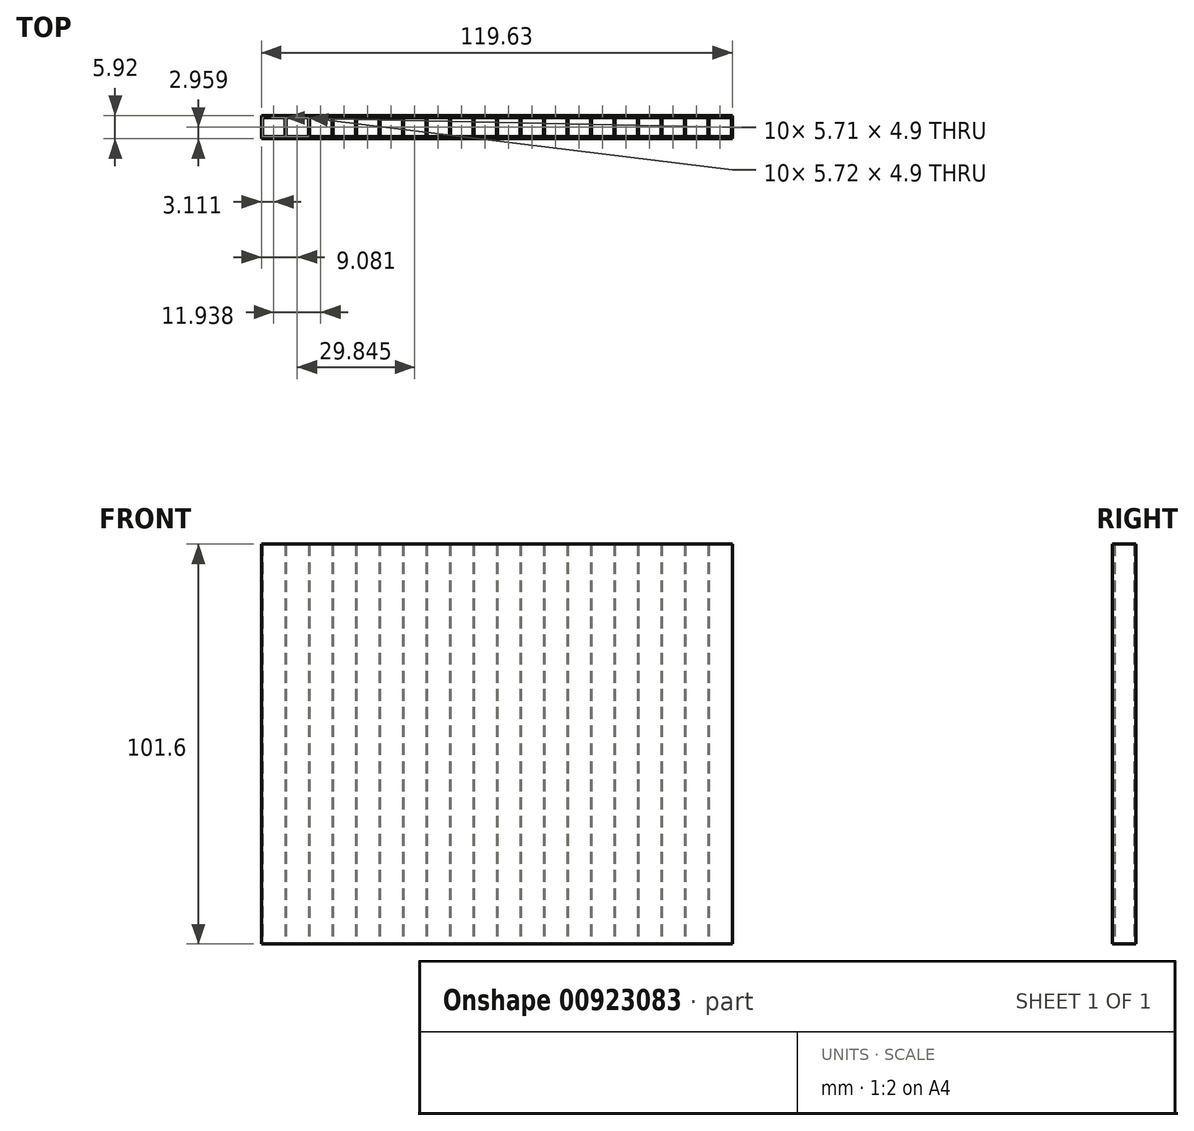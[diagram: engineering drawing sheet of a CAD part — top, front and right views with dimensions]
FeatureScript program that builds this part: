
annotation { "Feature Type Name" : "Feature", "Feature Type Description" : "" }
export const myFeature = defineFeature(function(context is Context, id is Id, definition is map)
    precondition{}
    {
        {
            var Q0;
            Q0=qCreatedBy(makeId("Top.planeOp"),FACE);
            var sketch = newSketch(context, id + "F0", { "sketchPlane" : qUnion([Q0])});
            skLineSegment(sketch, "E0", {"start": v(0, 0) * mm, "end": v(119.63, 0) * mm});
            skLineSegment(sketch, "E1", {"start": v(119.63, 0) * mm, "end": v(119.63, 5.92) * mm});
            skLineSegment(sketch, "E2", {"start": v(119.63, 5.92) * mm, "end": v(0, 5.92) * mm});
            skLineSegment(sketch, "E3", {"start": v(0, 5.92) * mm, "end": v(0, 0) * mm});
            skLineSegment(sketch, "E4.bottom", {"start": v(0.25, 5.41) * mm, "end": v(5.97, 5.41) * mm});
            skLineSegment(sketch, "E4.top", {"start": v(0.25, 0.5) * mm, "end": v(5.97, 0.5) * mm});
            skLineSegment(sketch, "E4.left", {"start": v(0.25, 5.41) * mm, "end": v(0.25, 0.5) * mm});
            skLineSegment(sketch, "E4.right", {"start": v(5.97, 5.41) * mm, "end": v(5.97, 0.5) * mm});
            skLineSegment(sketch, "E5.1.0.0", {"start": v(6.22, 5.41) * mm, "end": v(6.22, 0.5) * mm});
            skLineSegment(sketch, "E5.1.0.1", {"start": v(6.22, 5.41) * mm, "end": v(11.94, 5.41) * mm});
            skLineSegment(sketch, "E5.1.0.2", {"start": v(11.94, 5.41) * mm, "end": v(11.94, 0.5) * mm});
            skLineSegment(sketch, "E5.1.0.3", {"start": v(6.22, 0.5) * mm, "end": v(11.94, 0.5) * mm});
            skLineSegment(sketch, "E5.2.0.0", {"start": v(12.2, 5.41) * mm, "end": v(12.2, 0.5) * mm});
            skLineSegment(sketch, "E5.2.0.1", {"start": v(12.2, 5.41) * mm, "end": v(17.9, 5.41) * mm});
            skLineSegment(sketch, "E5.2.0.2", {"start": v(17.9, 5.41) * mm, "end": v(17.9, 0.5) * mm});
            skLineSegment(sketch, "E5.2.0.3", {"start": v(12.2, 0.5) * mm, "end": v(17.9, 0.5) * mm});
            skLineSegment(sketch, "E5.3.0.0", {"start": v(18.16, 5.41) * mm, "end": v(18.16, 0.5) * mm});
            skLineSegment(sketch, "E5.3.0.1", {"start": v(18.16, 5.41) * mm, "end": v(23.88, 5.41) * mm});
            skLineSegment(sketch, "E5.3.0.2", {"start": v(23.88, 5.41) * mm, "end": v(23.88, 0.5) * mm});
            skLineSegment(sketch, "E5.3.0.3", {"start": v(18.16, 0.5) * mm, "end": v(23.88, 0.5) * mm});
            skLineSegment(sketch, "E5.4.0.0", {"start": v(24.13, 5.41) * mm, "end": v(24.13, 0.5) * mm});
            skLineSegment(sketch, "E5.4.0.1", {"start": v(24.13, 5.41) * mm, "end": v(29.85, 5.41) * mm});
            skLineSegment(sketch, "E5.4.0.2", {"start": v(29.85, 5.41) * mm, "end": v(29.85, 0.5) * mm});
            skLineSegment(sketch, "E5.4.0.3", {"start": v(24.13, 0.5) * mm, "end": v(29.85, 0.5) * mm});
            skLineSegment(sketch, "E5.5.0.0", {"start": v(30.1, 5.41) * mm, "end": v(30.1, 0.5) * mm});
            skLineSegment(sketch, "E5.5.0.1", {"start": v(30.1, 5.41) * mm, "end": v(35.81, 5.41) * mm});
            skLineSegment(sketch, "E5.5.0.2", {"start": v(35.81, 5.41) * mm, "end": v(35.81, 0.5) * mm});
            skLineSegment(sketch, "E5.5.0.3", {"start": v(30.1, 0.5) * mm, "end": v(35.81, 0.5) * mm});
            skLineSegment(sketch, "E5.6.0.0", {"start": v(36.07, 5.41) * mm, "end": v(36.07, 0.5) * mm});
            skLineSegment(sketch, "E5.6.0.1", {"start": v(36.07, 5.41) * mm, "end": v(41.78, 5.41) * mm});
            skLineSegment(sketch, "E5.6.0.2", {"start": v(41.78, 5.41) * mm, "end": v(41.78, 0.5) * mm});
            skLineSegment(sketch, "E5.6.0.3", {"start": v(36.07, 0.5) * mm, "end": v(41.78, 0.5) * mm});
            skLineSegment(sketch, "E5.7.0.0", {"start": v(42.04, 5.41) * mm, "end": v(42.04, 0.5) * mm});
            skLineSegment(sketch, "E5.7.0.1", {"start": v(42.04, 5.41) * mm, "end": v(47.75, 5.41) * mm});
            skLineSegment(sketch, "E5.7.0.2", {"start": v(47.75, 5.41) * mm, "end": v(47.75, 0.5) * mm});
            skLineSegment(sketch, "E5.7.0.3", {"start": v(42.04, 0.5) * mm, "end": v(47.75, 0.5) * mm});
            skLineSegment(sketch, "E5.8.0.0", {"start": v(48, 5.41) * mm, "end": v(48, 0.5) * mm});
            skLineSegment(sketch, "E5.8.0.1", {"start": v(48, 5.41) * mm, "end": v(53.72, 5.41) * mm});
            skLineSegment(sketch, "E5.8.0.2", {"start": v(53.72, 5.41) * mm, "end": v(53.72, 0.5) * mm});
            skLineSegment(sketch, "E5.8.0.3", {"start": v(48, 0.5) * mm, "end": v(53.72, 0.5) * mm});
            skLineSegment(sketch, "E5.9.0.0", {"start": v(53.98, 5.41) * mm, "end": v(53.98, 0.5) * mm});
            skLineSegment(sketch, "E5.9.0.1", {"start": v(53.98, 5.41) * mm, "end": v(59.7, 5.41) * mm});
            skLineSegment(sketch, "E5.9.0.2", {"start": v(59.7, 5.41) * mm, "end": v(59.7, 0.5) * mm});
            skLineSegment(sketch, "E5.9.0.3", {"start": v(53.98, 0.5) * mm, "end": v(59.7, 0.5) * mm});
            skLineSegment(sketch, "E5.10.0.0", {"start": v(59.94, 5.41) * mm, "end": v(59.94, 0.5) * mm});
            skLineSegment(sketch, "E5.10.0.1", {"start": v(59.94, 5.41) * mm, "end": v(65.66, 5.41) * mm});
            skLineSegment(sketch, "E5.10.0.2", {"start": v(65.66, 5.41) * mm, "end": v(65.66, 0.5) * mm});
            skLineSegment(sketch, "E5.10.0.3", {"start": v(59.94, 0.5) * mm, "end": v(65.66, 0.5) * mm});
            skLineSegment(sketch, "E5.11.0.0", {"start": v(65.91, 5.41) * mm, "end": v(65.91, 0.5) * mm});
            skLineSegment(sketch, "E5.11.0.1", {"start": v(65.91, 5.41) * mm, "end": v(71.63, 5.41) * mm});
            skLineSegment(sketch, "E5.11.0.2", {"start": v(71.63, 5.41) * mm, "end": v(71.63, 0.5) * mm});
            skLineSegment(sketch, "E5.11.0.3", {"start": v(65.91, 0.5) * mm, "end": v(71.63, 0.5) * mm});
            skLineSegment(sketch, "E5.12.0.0", {"start": v(71.88, 5.41) * mm, "end": v(71.88, 0.5) * mm});
            skLineSegment(sketch, "E5.12.0.1", {"start": v(71.88, 5.41) * mm, "end": v(77.6, 5.41) * mm});
            skLineSegment(sketch, "E5.12.0.2", {"start": v(77.6, 5.41) * mm, "end": v(77.6, 0.5) * mm});
            skLineSegment(sketch, "E5.12.0.3", {"start": v(71.88, 0.5) * mm, "end": v(77.6, 0.5) * mm});
            skLineSegment(sketch, "E5.13.0.0", {"start": v(77.85, 5.41) * mm, "end": v(77.85, 0.5) * mm});
            skLineSegment(sketch, "E5.13.0.1", {"start": v(77.85, 5.41) * mm, "end": v(83.57, 5.41) * mm});
            skLineSegment(sketch, "E5.13.0.2", {"start": v(83.57, 5.41) * mm, "end": v(83.57, 0.5) * mm});
            skLineSegment(sketch, "E5.13.0.3", {"start": v(77.85, 0.5) * mm, "end": v(83.57, 0.5) * mm});
            skLineSegment(sketch, "E5.14.0.0", {"start": v(83.82, 5.41) * mm, "end": v(83.82, 0.5) * mm});
            skLineSegment(sketch, "E5.14.0.1", {"start": v(83.82, 5.41) * mm, "end": v(89.53, 5.41) * mm});
            skLineSegment(sketch, "E5.14.0.2", {"start": v(89.53, 5.41) * mm, "end": v(89.53, 0.5) * mm});
            skLineSegment(sketch, "E5.14.0.3", {"start": v(83.82, 0.5) * mm, "end": v(89.53, 0.5) * mm});
            skLineSegment(sketch, "E5.15.0.0", {"start": v(89.79, 5.41) * mm, "end": v(89.79, 0.5) * mm});
            skLineSegment(sketch, "E5.15.0.1", {"start": v(89.79, 5.41) * mm, "end": v(95.5, 5.41) * mm});
            skLineSegment(sketch, "E5.15.0.2", {"start": v(95.5, 5.41) * mm, "end": v(95.5, 0.5) * mm});
            skLineSegment(sketch, "E5.15.0.3", {"start": v(89.79, 0.5) * mm, "end": v(95.5, 0.5) * mm});
            skLineSegment(sketch, "E5.16.0.0", {"start": v(95.76, 5.41) * mm, "end": v(95.76, 0.5) * mm});
            skLineSegment(sketch, "E5.16.0.1", {"start": v(95.76, 5.41) * mm, "end": v(101.47, 5.41) * mm});
            skLineSegment(sketch, "E5.16.0.2", {"start": v(101.47, 5.41) * mm, "end": v(101.47, 0.5) * mm});
            skLineSegment(sketch, "E5.16.0.3", {"start": v(95.76, 0.5) * mm, "end": v(101.47, 0.5) * mm});
            skLineSegment(sketch, "E5.17.0.0", {"start": v(101.73, 5.41) * mm, "end": v(101.73, 0.5) * mm});
            skLineSegment(sketch, "E5.17.0.1", {"start": v(101.73, 5.41) * mm, "end": v(107.44, 5.41) * mm});
            skLineSegment(sketch, "E5.17.0.2", {"start": v(107.44, 5.41) * mm, "end": v(107.44, 0.5) * mm});
            skLineSegment(sketch, "E5.17.0.3", {"start": v(101.73, 0.5) * mm, "end": v(107.44, 0.5) * mm});
            skLineSegment(sketch, "E5.18.0.0", {"start": v(107.7, 5.41) * mm, "end": v(107.7, 0.5) * mm});
            skLineSegment(sketch, "E5.18.0.1", {"start": v(107.7, 5.41) * mm, "end": v(113.41, 5.41) * mm});
            skLineSegment(sketch, "E5.18.0.2", {"start": v(113.41, 5.41) * mm, "end": v(113.41, 0.5) * mm});
            skLineSegment(sketch, "E5.18.0.3", {"start": v(107.7, 0.5) * mm, "end": v(113.41, 0.5) * mm});
            skLineSegment(sketch, "E5.19.0.0", {"start": v(113.67, 5.41) * mm, "end": v(113.67, 0.5) * mm});
            skLineSegment(sketch, "E5.19.0.1", {"start": v(113.67, 5.41) * mm, "end": v(119.38, 5.41) * mm});
            skLineSegment(sketch, "E5.19.0.2", {"start": v(119.38, 5.41) * mm, "end": v(119.38, 0.5) * mm});
            skLineSegment(sketch, "E5.19.0.3", {"start": v(113.67, 0.5) * mm, "end": v(119.38, 0.5) * mm});
            skLineSegment(sketch, "E5.direction1", {"start": v(0.25, 0.5) * mm, "end": v(6.22, 0.5) * mm, "construction": true});
            skSolve(sketch);
        }
        {
            var Q0;
            Q0=makeQuery(id+"F0.imprint","IMPRINT",FACE,{"disambiguationData":[TD([[makeQuery(id+"F0.imprint","IMPRINT",EDGE,{"derivedFrom":sQuery(id+"F0.wireOp",EDGE,"E0")}),1.0]])]});
            extrude(context, id + "F1", {"entities" : qUnion([Q0]), "depth" : 76.2 * mm, "offsetDistance" : 25.4 * mm});
        }
        {
            var Q0;
            Q0=makeQuery(id+"F1.opExtrude","CAP_FACE",FACE,{"disambiguationData":[OSD([sQuery(id+"F0.wireOp",EDGE,"E0"),sQuery(id+"F0.wireOp",EDGE,"E1"),sQuery(id+"F0.wireOp",EDGE,"E2"),sQuery(id+"F0.wireOp",EDGE,"E3"),sQuery(id+"F0.wireOp",EDGE,"E4.bottom"),sQuery(id+"F0.wireOp",EDGE,"E4.top"),sQuery(id+"F0.wireOp",EDGE,"E4.left"),sQuery(id+"F0.wireOp",EDGE,"E4.right"),sQuery(id+"F0.wireOp",EDGE,"E5.1.0.0"),sQuery(id+"F0.wireOp",EDGE,"E5.1.0.1"),sQuery(id+"F0.wireOp",EDGE,"E5.1.0.2"),sQuery(id+"F0.wireOp",EDGE,"E5.1.0.3"),sQuery(id+"F0.wireOp",EDGE,"E5.2.0.0"),sQuery(id+"F0.wireOp",EDGE,"E5.2.0.1"),sQuery(id+"F0.wireOp",EDGE,"E5.2.0.2"),sQuery(id+"F0.wireOp",EDGE,"E5.2.0.3"),sQuery(id+"F0.wireOp",EDGE,"E5.3.0.0"),sQuery(id+"F0.wireOp",EDGE,"E5.3.0.1"),sQuery(id+"F0.wireOp",EDGE,"E5.3.0.2"),sQuery(id+"F0.wireOp",EDGE,"E5.3.0.3"),sQuery(id+"F0.wireOp",EDGE,"E5.4.0.0"),sQuery(id+"F0.wireOp",EDGE,"E5.4.0.1"),sQuery(id+"F0.wireOp",EDGE,"E5.4.0.2"),sQuery(id+"F0.wireOp",EDGE,"E5.4.0.3"),sQuery(id+"F0.wireOp",EDGE,"E5.5.0.0"),sQuery(id+"F0.wireOp",EDGE,"E5.5.0.1"),sQuery(id+"F0.wireOp",EDGE,"E5.5.0.2"),sQuery(id+"F0.wireOp",EDGE,"E5.5.0.3"),sQuery(id+"F0.wireOp",EDGE,"E5.6.0.0"),sQuery(id+"F0.wireOp",EDGE,"E5.6.0.1"),sQuery(id+"F0.wireOp",EDGE,"E5.6.0.2"),sQuery(id+"F0.wireOp",EDGE,"E5.6.0.3"),sQuery(id+"F0.wireOp",EDGE,"E5.7.0.0"),sQuery(id+"F0.wireOp",EDGE,"E5.7.0.1"),sQuery(id+"F0.wireOp",EDGE,"E5.7.0.2"),sQuery(id+"F0.wireOp",EDGE,"E5.7.0.3"),sQuery(id+"F0.wireOp",EDGE,"E5.8.0.0"),sQuery(id+"F0.wireOp",EDGE,"E5.8.0.1"),sQuery(id+"F0.wireOp",EDGE,"E5.8.0.2"),sQuery(id+"F0.wireOp",EDGE,"E5.8.0.3"),sQuery(id+"F0.wireOp",EDGE,"E5.9.0.0"),sQuery(id+"F0.wireOp",EDGE,"E5.9.0.1"),sQuery(id+"F0.wireOp",EDGE,"E5.9.0.2"),sQuery(id+"F0.wireOp",EDGE,"E5.9.0.3"),sQuery(id+"F0.wireOp",EDGE,"E5.10.0.0"),sQuery(id+"F0.wireOp",EDGE,"E5.10.0.1"),sQuery(id+"F0.wireOp",EDGE,"E5.10.0.2"),sQuery(id+"F0.wireOp",EDGE,"E5.10.0.3"),sQuery(id+"F0.wireOp",EDGE,"E5.11.0.0"),sQuery(id+"F0.wireOp",EDGE,"E5.11.0.1"),sQuery(id+"F0.wireOp",EDGE,"E5.11.0.2"),sQuery(id+"F0.wireOp",EDGE,"E5.11.0.3"),sQuery(id+"F0.wireOp",EDGE,"E5.12.0.0"),sQuery(id+"F0.wireOp",EDGE,"E5.12.0.1"),sQuery(id+"F0.wireOp",EDGE,"E5.12.0.2"),sQuery(id+"F0.wireOp",EDGE,"E5.12.0.3"),sQuery(id+"F0.wireOp",EDGE,"E5.13.0.0"),sQuery(id+"F0.wireOp",EDGE,"E5.13.0.1"),sQuery(id+"F0.wireOp",EDGE,"E5.13.0.2"),sQuery(id+"F0.wireOp",EDGE,"E5.13.0.3"),sQuery(id+"F0.wireOp",EDGE,"E5.14.0.0"),sQuery(id+"F0.wireOp",EDGE,"E5.14.0.1"),sQuery(id+"F0.wireOp",EDGE,"E5.14.0.2"),sQuery(id+"F0.wireOp",EDGE,"E5.14.0.3"),sQuery(id+"F0.wireOp",EDGE,"E5.15.0.0"),sQuery(id+"F0.wireOp",EDGE,"E5.15.0.1"),sQuery(id+"F0.wireOp",EDGE,"E5.15.0.2"),sQuery(id+"F0.wireOp",EDGE,"E5.15.0.3"),sQuery(id+"F0.wireOp",EDGE,"E5.16.0.0"),sQuery(id+"F0.wireOp",EDGE,"E5.16.0.1"),sQuery(id+"F0.wireOp",EDGE,"E5.16.0.2"),sQuery(id+"F0.wireOp",EDGE,"E5.16.0.3"),sQuery(id+"F0.wireOp",EDGE,"E5.17.0.0"),sQuery(id+"F0.wireOp",EDGE,"E5.17.0.1"),sQuery(id+"F0.wireOp",EDGE,"E5.17.0.2"),sQuery(id+"F0.wireOp",EDGE,"E5.17.0.3"),sQuery(id+"F0.wireOp",EDGE,"E5.18.0.0"),sQuery(id+"F0.wireOp",EDGE,"E5.18.0.1"),sQuery(id+"F0.wireOp",EDGE,"E5.18.0.2"),sQuery(id+"F0.wireOp",EDGE,"E5.18.0.3"),sQuery(id+"F0.wireOp",EDGE,"E5.19.0.0"),sQuery(id+"F0.wireOp",EDGE,"E5.19.0.1"),sQuery(id+"F0.wireOp",EDGE,"E5.19.0.2"),sQuery(id+"F0.wireOp",EDGE,"E5.19.0.3")])],"isStart":true});
            extrude(context, id + "F2", {"entities" : qUnion([Q0]), "operationType" : NewBodyOperationType.ADD, "depth" : 25.4 * mm, "offsetDistance" : 25.4 * mm});
        }
    });
